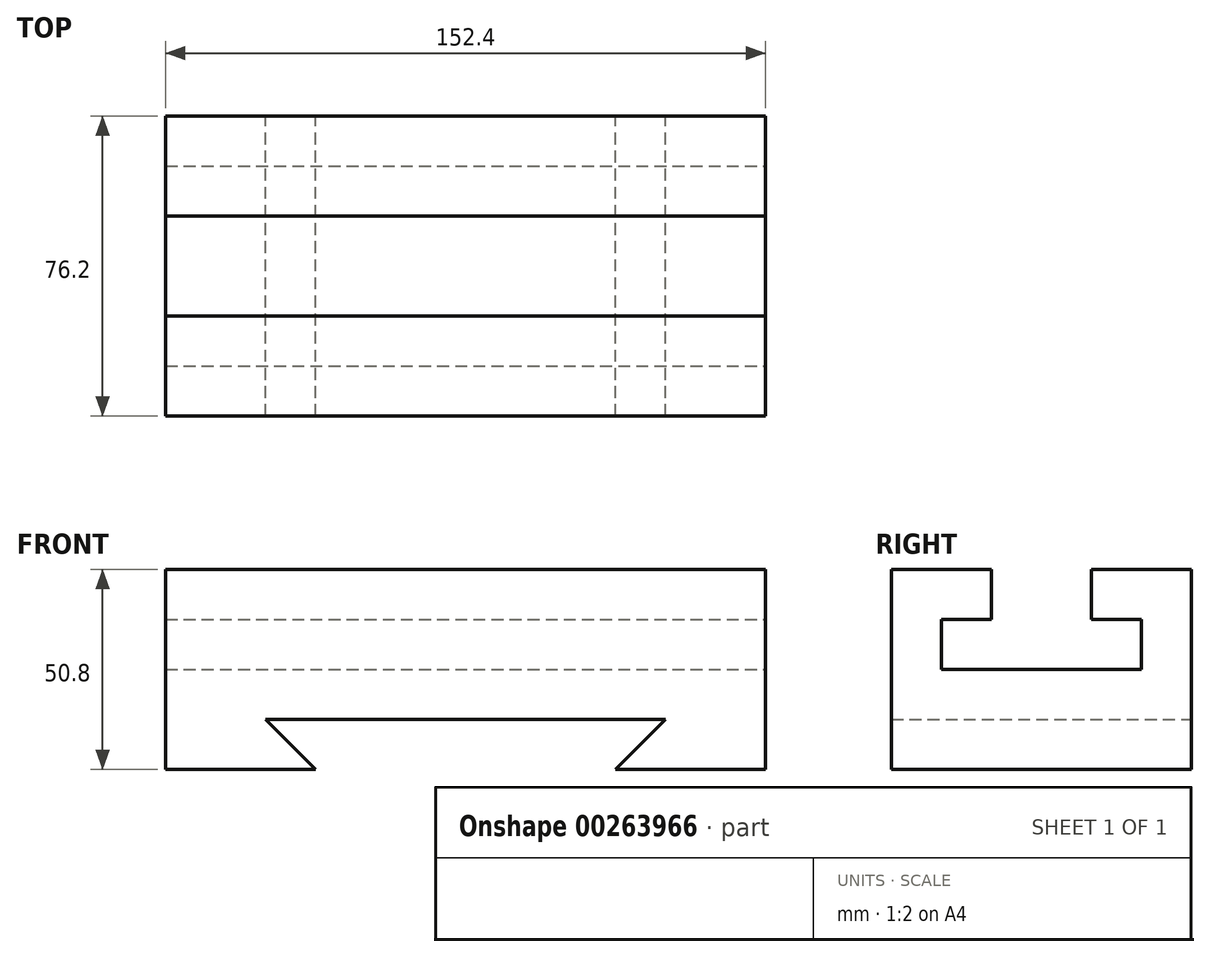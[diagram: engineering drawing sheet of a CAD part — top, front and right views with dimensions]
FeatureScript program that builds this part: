
annotation { "Feature Type Name" : "Feature", "Feature Type Description" : "" }
export const myFeature = defineFeature(function(context is Context, id is Id, definition is map)
    precondition{}
    {
        {
            var Q0;
            Q0=qCreatedBy(makeId("Front.planeOp"),FACE);
            var sketch = newSketch(context, id + "F0", { "sketchPlane" : qUnion([Q0])});
            skLineSegment(sketch, "E0", {"start": v(0, 0) * mm, "end": v(0, 50.8) * mm});
            skLineSegment(sketch, "E1", {"start": v(0, 50.8) * mm, "end": v(152.4, 50.8) * mm});
            skLineSegment(sketch, "E2", {"start": v(152.4, 50.8) * mm, "end": v(152.4, 0) * mm});
            skLineSegment(sketch, "E3", {"start": v(152.4, 0) * mm, "end": v(114.3, 0) * mm});
            skLineSegment(sketch, "E4", {"start": v(38.1, 0) * mm, "end": v(0, 0) * mm});
            skLineSegment(sketch, "E5", {"start": v(0, 0) * mm, "end": v(0, 12.7) * mm, "construction": true});
            skLineSegment(sketch, "E6", {"start": v(0, 12.7) * mm, "end": v(25.4, 12.7) * mm, "construction": true});
            skLineSegment(sketch, "E7", {"start": v(152.4, 0) * mm, "end": v(152.4, 12.7) * mm, "construction": true});
            skLineSegment(sketch, "E8", {"start": v(152.4, 12.7) * mm, "end": v(127, 12.7) * mm, "construction": true});
            skLineSegment(sketch, "E9", {"start": v(38.1, 0) * mm, "end": v(25.4, 12.7) * mm});
            skLineSegment(sketch, "E10", {"start": v(127, 12.7) * mm, "end": v(114.3, 0) * mm});
            skLineSegment(sketch, "E11", {"start": v(25.4, 12.7) * mm, "end": v(127, 12.7) * mm});
            skSolve(sketch);
        }
        {
            var Q0;
            Q0=makeQuery(id+"F0.imprint","IMPRINT",FACE,{"disambiguationData":[TD([[makeQuery(id+"F0.imprint","IMPRINT",EDGE,{"derivedFrom":sQuery(id+"F0.wireOp",EDGE,"E0")}),-1.0]])]});
            extrude(context, id + "F1", {"entities" : qUnion([Q0]), "depth" : 76.2 * mm});
        }
        {
            var Q0;
            Q0=makeQuery(id+"F1.opExtrude","SWEPT_FACE",FACE,{"disambiguationData":[OSD([sQuery(id+"F0.wireOp",EDGE,"E2")])]});
            var sketch = newSketch(context, id + "F2", { "sketchPlane" : qUnion([Q0])});
            skLineSegment(sketch, "E12", {"start": v(-76.2, 50.8) * mm, "end": v(-50.8, 50.8) * mm, "construction": true});
            skLineSegment(sketch, "E13", {"start": v(-50.8, 50.8) * mm, "end": v(-50.8, 38.1) * mm});
            skLineSegment(sketch, "E14", {"start": v(-50.8, 38.1) * mm, "end": v(-63.5, 38.1) * mm});
            skLineSegment(sketch, "E15", {"start": v(-63.5, 38.1) * mm, "end": v(-63.5, 25.4) * mm});
            skLineSegment(sketch, "E16", {"start": v(-63.5, 25.4) * mm, "end": v(-12.7, 25.4) * mm});
            skLineSegment(sketch, "E17", {"start": v(-12.7, 25.4) * mm, "end": v(-12.7, 38.1) * mm});
            skLineSegment(sketch, "E18", {"start": v(-12.7, 38.1) * mm, "end": v(-25.4, 38.1) * mm});
            skLineSegment(sketch, "E19", {"start": v(-25.4, 38.1) * mm, "end": v(-25.4, 50.8) * mm});
            skLineSegment(sketch, "E20", {"start": v(-25.4, 50.8) * mm, "end": v(0, 50.8) * mm, "construction": true});
            skSolve(sketch);
        }
        {
            var Q0;
            {var subQ0=sQuery(id+"F2.wireOp",EDGE,"E13");Q0=makeQuery(id+"F2.imprint","IMPRINT",FACE,{"disambiguationData":[TD([[makeQuery(id+"F2.imprint","IMPRINT",EDGE,{"derivedFrom":subQ0}),1.0]])]});}
            extrude(context, id + "F3", {"entities" : qUnion([Q0]), "operationType" : NewBodyOperationType.REMOVE, "oppositeDirection" : true, "depth" : 152.4 * mm});
        }
    });
